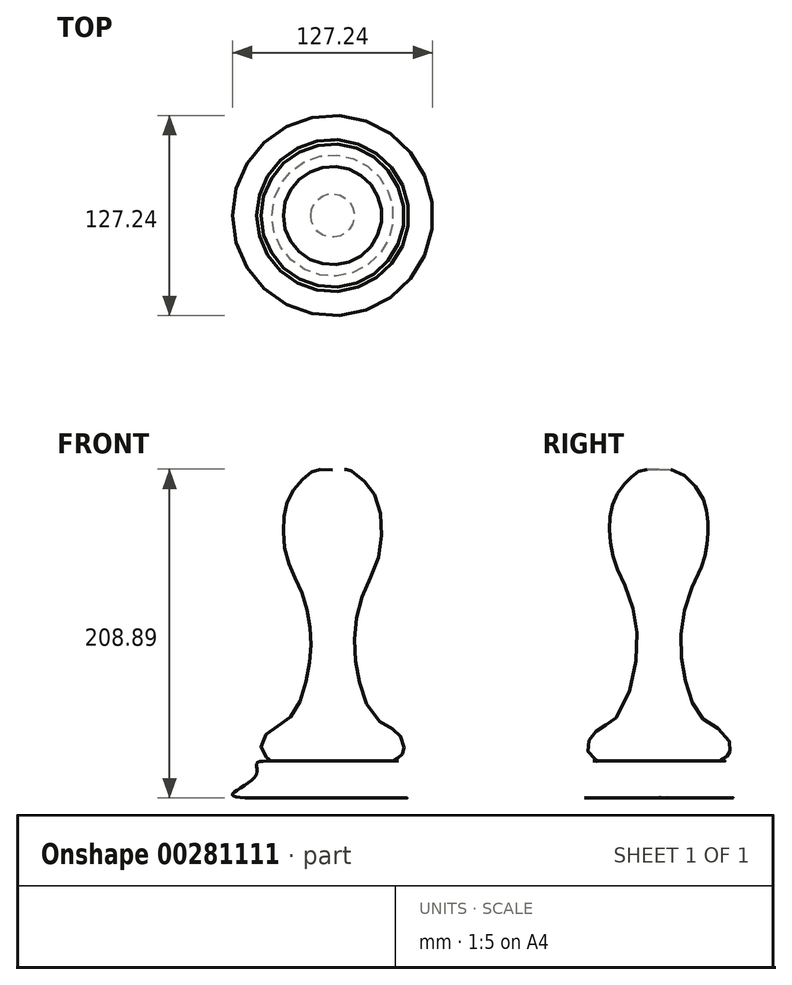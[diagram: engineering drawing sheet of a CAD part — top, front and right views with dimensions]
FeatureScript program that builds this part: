
annotation { "Feature Type Name" : "Feature", "Feature Type Description" : "" }
export const myFeature = defineFeature(function(context is Context, id is Id, definition is map)
    precondition{}
    {
        {
            var Q0;
            Q0=qCreatedBy(makeId("Front.planeOp"),FACE);
            var sketch = newSketch(context, id + "F0", { "sketchPlane" : qUnion([Q0])});
            skLineSegment(sketch, "E0", {"start": v(0, 117.83) * mm, "end": v(0, -137.55) * mm, "construction": true});
            skFitSpline(sketch, "E1", {"points": [v(0, 117.83) * mm, v(-10.19, 117.83) * mm, v(-18.7, 112.16) * mm, v(-28, 99.2) * mm, v(-31.25, 82.6) * mm, v(-28.6, 60.48) * mm, v(-20.13, 41.04) * mm, v(-14.15, 15.62) * mm, v(-15.65, -10.3) * mm, v(-27.11, -39.7) * mm, v(-42.07, -50.18) * mm, v(-44.06, -63.14) * mm, v(-38.58, -67.13) * mm, v(-47.55, -68.12) * mm, v(-48.55, -76.1) * mm, v(-63.5, -88.06) * mm, v(0, -90.06) * mm], "startDerivative": vector(-365.88, 0) * mm, "endDerivative": vector(891.87, 0) * mm});
            skLineSegment(sketch, "E2", {"start": v(0, 117.83) * mm, "end": v(0, -90.06) * mm});
            skSolve(sketch);
        }
        {
            var Q0;
            Q0=makeQuery(id+"F0.imprint","IMPRINT",FACE,{"disambiguationData":[TD([[makeQuery(id+"F0.imprint","IMPRINT",EDGE,{"derivedFrom":sQuery(id+"F0.wireOp",EDGE,"E1")}),1.0]])]});
            var Q1;
            Q1=sQuery(id+"F0.wireOp",EDGE,"E0");
            revolve(context, id + "F1", {"entities" : qUnion([Q0]), "axis" : qUnion([Q1]), "revolveType" : RevolveType.FULL});
        }
    });
